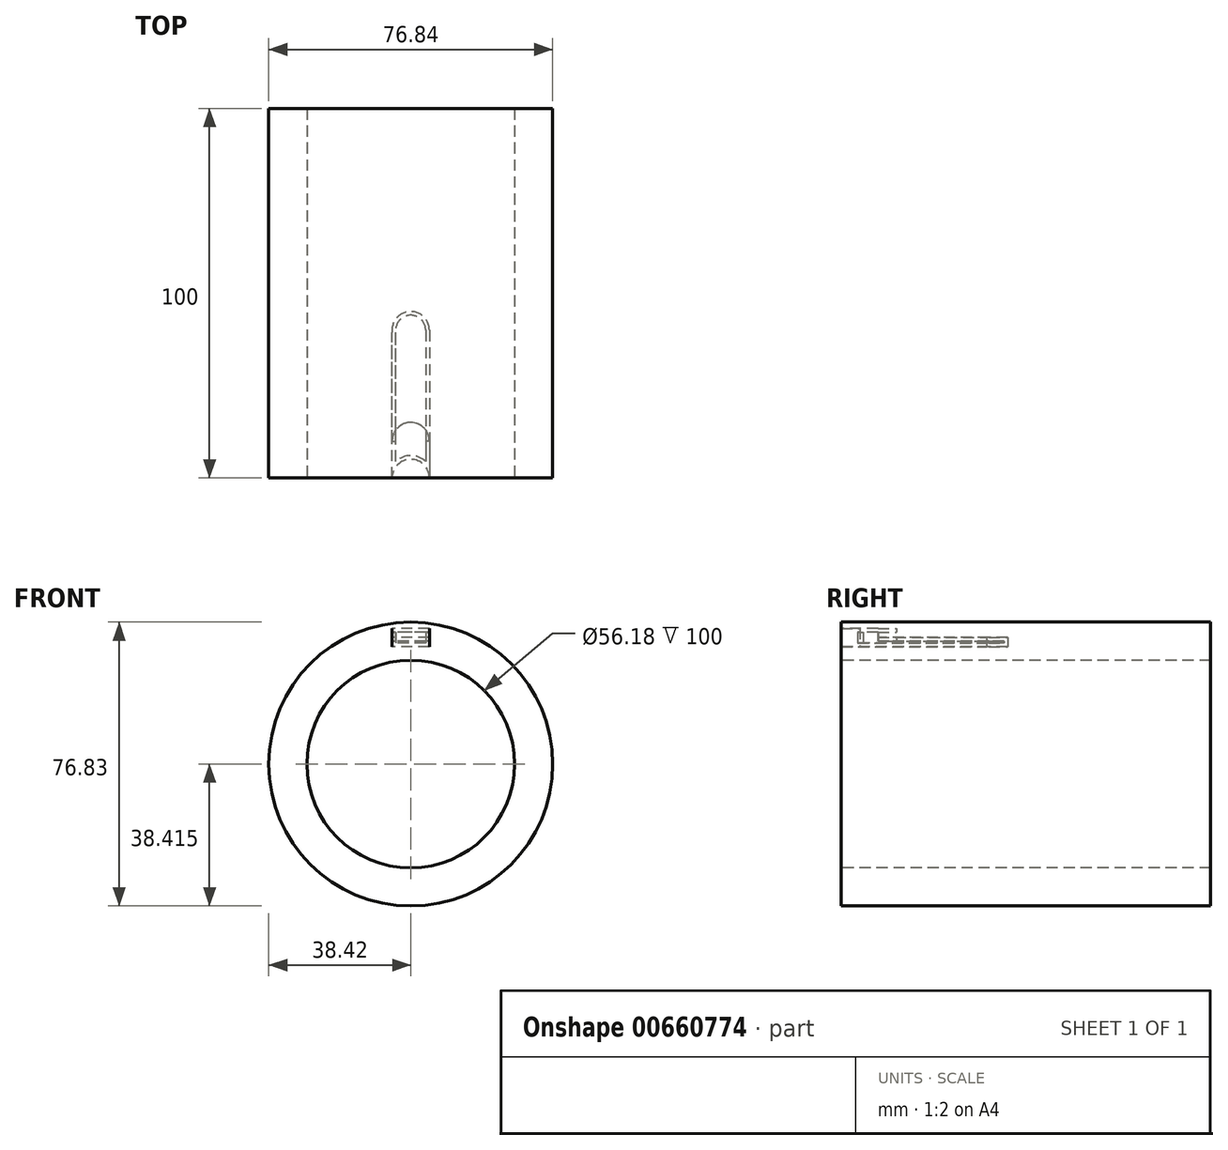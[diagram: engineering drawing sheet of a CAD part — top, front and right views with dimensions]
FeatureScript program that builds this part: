
annotation { "Feature Type Name" : "Feature", "Feature Type Description" : "" }
export const myFeature = defineFeature(function(context is Context, id is Id, definition is map)
    precondition{}
    {
        {
            var Q0;
            Q0=qCreatedBy(makeId("Top.planeOp"),FACE);
            var sketch = newSketch(context, id + "F0", { "sketchPlane" : qUnion([Q0])});
            skLineSegment(sketch, "E0", {"start": v(-5.04, 0) * mm, "end": v(-5.04, 39.38) * mm});
            skLineSegment(sketch, "E1", {"start": v(5.04, 40) * mm, "end": v(5.04, 0) * mm});
            skArc(sketch, "E2", {"start": v(5.04, 40) * mm, "mid": v(-0.33, 45.05) * mm, "end": v(-5.04, 39.38) * mm});
            skArc(sketch, "E3", {"start": v(5.04, 0) * mm, "mid": v(0, 5.04) * mm, "end": v(-5.04, 0) * mm});
            skLineSegment(sketch, "E4", {"start": v(-5.04, 0) * mm, "end": v(-5.04, 10) * mm});
            skLineSegment(sketch, "E5", {"start": v(5.04, 0) * mm, "end": v(5.04, 10) * mm});
            skArc(sketch, "E6", {"start": v(5.04, 10) * mm, "mid": v(0, 15.04) * mm, "end": v(-5.04, 10) * mm});
            skSolve(sketch);
        }
        {
            var Q0;
            Q0=makeQuery(id+"F0.imprint","IMPRINT",FACE,{"disambiguationData":[TD([[makeQuery(id+"F0.imprint","IMPRINT",EDGE,{"derivedFrom":sQuery(id+"F0.wireOp",EDGE,"E3")}),-1.0]])]});
            extrude(context, id + "F1", {"entities" : qUnion([Q0]), "depth" : 5 * mm, "offsetDistance" : 25 * mm});
        }
        {
            var Q0;
            Q0 = qSketchRegion(id + "F0", true);
            extrude(context, id + "F2", {"entities" : qUnion([Q0]), "operationType" : NewBodyOperationType.ADD, "depth" : 2.5 * mm, "offsetDistance" : 25 * mm});
        }
        {
            var Q0;
            Q0=makeQuery(id+"F1.opExtrude","SWEPT_FACE",FACE,{"disambiguationData":[OSD([sQuery(id+"F0.wireOp",EDGE,"E6")])]});
            shell(context, id + "F3", {"entities" : qUnion([Q0]), "thickness" : 1 * mm});
        }
        {
            var Q0;
            Q0=qCreatedBy(makeId("Front.planeOp"),FACE);
            var sketch = newSketch(context, id + "F4", { "sketchPlane" : qUnion([Q0])});
            skCircle(sketch, "E7", {"center": v(0, -31.74) * mm, "radius": 38.42 * mm});
            skCircle(sketch, "E8", {"center": v(0, -31.74) * mm, "radius": 28.09 * mm});
            skLineSegment(sketch, "E9", {"start": v(0, 0) * mm, "end": v(0, -76.23) * mm});
            skLineSegment(sketch, "E10", {"start": v(-40.79, -31.74) * mm, "end": v(58.71, -31.74) * mm});
            skSolve(sketch);
        }
        {
            var Q0;
            {var subQ5=sQuery(id+"F4.wireOp",EDGE,"E7");var subQ6=makeQuery(id+"F4.imprint","INTERSECT",VERTEX,{"derivedFrom":[subQ5,sQuery(id+"F4.wireOp",EDGE,"UcgWSMXG-0Yw3-K6XL-519j-ZLKteTKPt0x1")]});Q0=makeQuery(id+"F4.imprint","IMPRINT",FACE,{"disambiguationData":[TD([[makeQuery(id+"F4.imprint","IMPRINT",EDGE,{"disambiguationData":[TD([[subQ6,1.0]])],"derivedFrom":subQ5}),1.0]])]});}
            var Q1;
            {var subQ0=sQuery(id+"F4.wireOp",EDGE,"E10");var subQ1=sQuery(id+"F4.wireOp",EDGE,"E7");var subQ2=makeQuery(id+"F4.imprint","INTERSECT",VERTEX,{"disambiguationData":[OD(0.0)],"derivedFrom":[subQ1,subQ0]});Q1=makeQuery(id+"F4.imprint","IMPRINT",FACE,{"disambiguationData":[TD([[makeQuery(id+"F4.imprint","IMPRINT",EDGE,{"disambiguationData":[TD([[subQ2,1.0]])],"derivedFrom":subQ1}),1.0]])]});}
            var Q2;
            {var subQ1=sQuery(id+"F4.wireOp",EDGE,"E7");var subQ5=makeQuery(id+"F4.imprint","INTERSECT",VERTEX,{"derivedFrom":[subQ1,sQuery(id+"F4.wireOp",EDGE,"FcwjgSPD-3s7T-1KSm-IO48-xDtWDZBX26w0")]});Q2=makeQuery(id+"F4.imprint","IMPRINT",FACE,{"disambiguationData":[TD([[makeQuery(id+"F4.imprint","IMPRINT",EDGE,{"disambiguationData":[TD([[subQ5,1.0]])],"derivedFrom":subQ1}),1.0]])]});}
            extrude(context, id + "F5", {"entities" : qUnion([Q0, Q1, Q2]), "oppositeDirection" : true, "depth" : 100 * mm, "offsetDistance" : 25 * mm});
        }
    });
